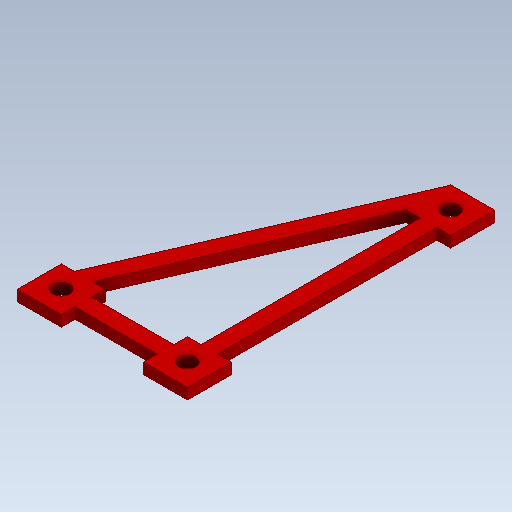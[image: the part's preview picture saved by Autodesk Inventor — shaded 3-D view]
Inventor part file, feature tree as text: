
AUTODESK INVENTOR PART (.ipt)
format: ipt  version: 2020 (Build 240168000, 168)  size: 152,064 bytes
history: native  units: mm
features: sketch x2, other x1, extrude x1
ambient origin geometry x8: Origin, YZ Plane, XZ Plane, XY Plane, X Axis, Y Axis, Z Axis, Center Point
bodies: Solid1 (feature_tree)
feature tree (4):
  other  "HexBodyV2.ipt"
  extrude  "Extrusion1"  Depth=10.0mm
  sketch  "Sketch14"  dims[d2=3.1mm d3=3.1mm d4=3.0mm d5=3.0mm d6=3.0mm d7=2.0mm d8=0.0mm]
  sketch  "Sketch2"  dims[d0=10.0mm d1=3.1mm]
